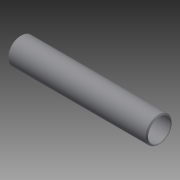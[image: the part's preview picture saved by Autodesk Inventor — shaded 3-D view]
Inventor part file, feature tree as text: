
AUTODESK INVENTOR PART (.ipt)
format: ipt  version: 2014 SP2 (Build 180246200, 246)  size: 140,288 bytes
history: native  units: in
note: dims shown in document units (in); Inventor stores cm internally (conversion verified against a paired STEP export)
features: other x42, revolve x1, sketch x1
ambient origin geometry x8: Origin, YZ Plane, XZ Plane, XY Plane, X Axis, Y Axis, Z Axis, Center Point
bodies: Solid1 (feature_tree)
feature tree (44):
  revolve  "Revolution1"  [1 undecoded]
  other  "cp1_XY"
  other  "cp1_YZ"
  other  "cp1_ZX"
  other  "cp1_X"
  other  "cp1_Y"
  other  "cp1_Z"
  other  "cp1_Center"
  other  "cp2_XY"
  other  "cp2_YZ"
  other  "cp2_ZX"
  other  "cp2_X"
  other  "cp2_Y"
  other  "cp2_Z"
  other  "cp2_Center"
  other  "cp3_XY"
  other  "cp3_YZ"
  other  "cp3_ZX"
  other  "cp3_X"
  other  "cp3_Y"
  other  "cp3_Z"
  other  "cp3_Center"
  other  "cp4_XY"
  other  "cp4_YZ"
  other  "cp4_ZX"
  other  "cp4_X"
  other  "cp4_Y"
  other  "cp4_Z"
  other  "cp4_Center"
  other  "tube_front_XY"
  other  "tube_front_YZ"
  other  "tube_front_ZX"
  other  "tube_front_X"
  other  "tube_front_Y"
  other  "tube_front_Z"
  other  "tube_front_Center"
  other  "tube_rear_XY"
  other  "tube_rear_YZ"
  other  "tube_rear_ZX"
  other  "tube_rear_X"
  other  "tube_rear_Y"
  other  "tube_rear_Z"
  other  "tube_rear_Center"
  sketch  "Sketch_1"  dims[d0=360.0deg]
note: 1 required parameter value undecoded (feature->parameter linkage not recoverable at this tier; creation-order binding heuristic only, values carry confidence <= 0.55)
